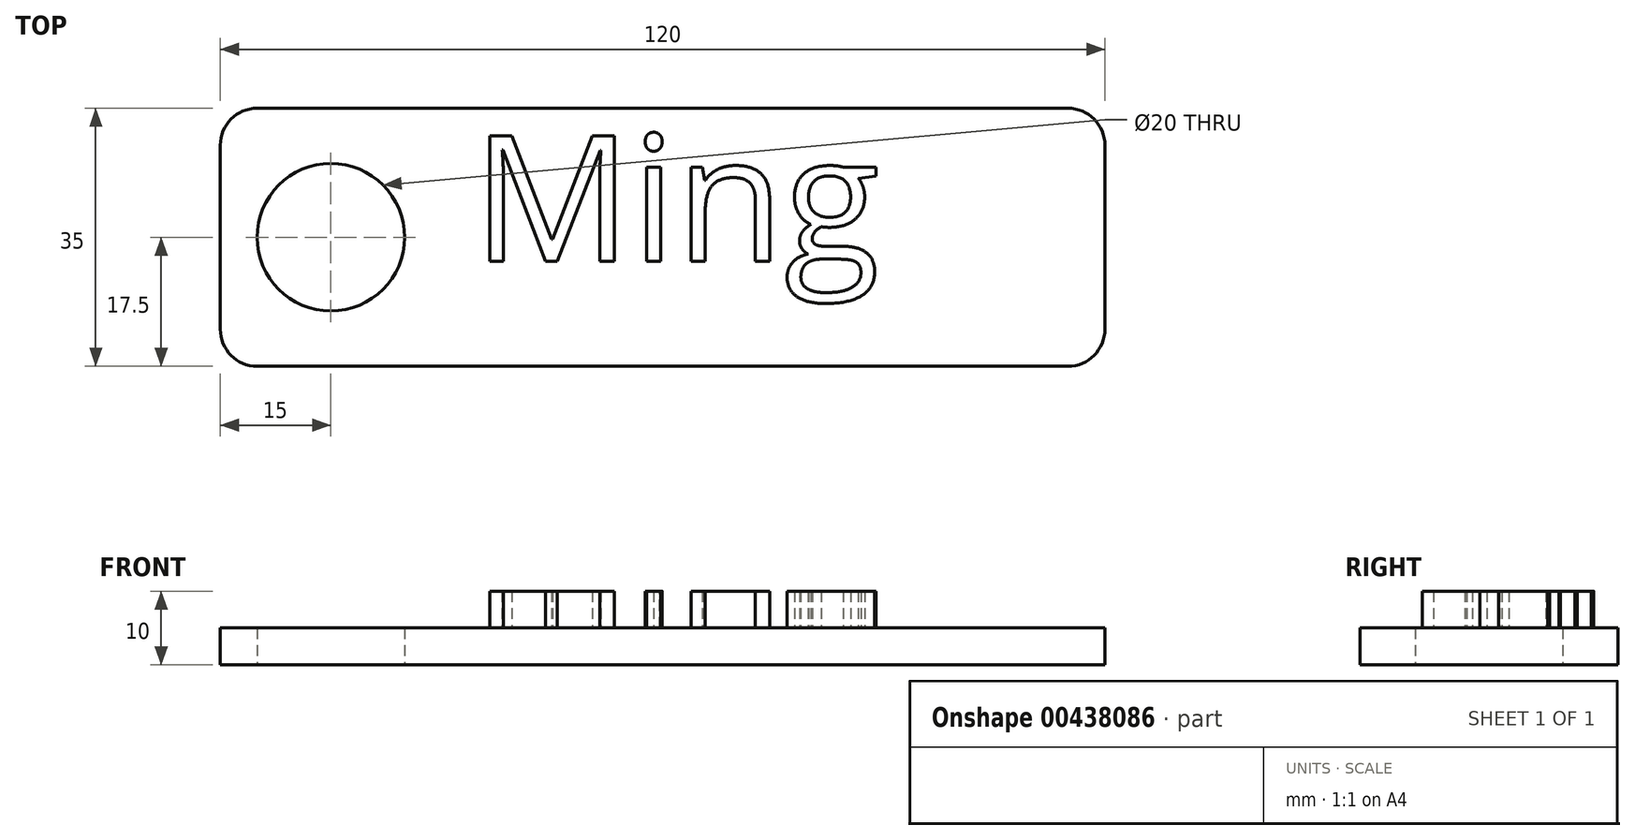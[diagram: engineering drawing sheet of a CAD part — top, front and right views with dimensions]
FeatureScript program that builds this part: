
annotation { "Feature Type Name" : "Feature", "Feature Type Description" : "" }
export const myFeature = defineFeature(function(context is Context, id is Id, definition is map)
    precondition{}
    {
        {
            var Q0;
            Q0=qCreatedBy(makeId("Top.planeOp"),FACE);
            var sketch = newSketch(context, id + "F0", { "sketchPlane" : qUnion([Q0])});
            skLineSegment(sketch, "E0.bottom", {"start": v(60, -17.5) * mm, "end": v(-60, -17.5) * mm});
            skLineSegment(sketch, "E0.top", {"start": v(60, 17.5) * mm, "end": v(-60, 17.5) * mm});
            skLineSegment(sketch, "E0.left", {"start": v(60, -17.5) * mm, "end": v(60, 17.5) * mm});
            skLineSegment(sketch, "E0.right", {"start": v(-60, -17.5) * mm, "end": v(-60, 17.5) * mm});
            skPoint(sketch, "E0.middle", {"position": v(0, 0) * mm});
            skCircle(sketch, "E1", {"center": v(-45, 0) * mm, "radius": 10 * mm});
            skSolve(sketch);
        }
        {
            var Q0;
            Q0=makeQuery(id+"F0.imprint","IMPRINT",FACE,{"disambiguationData":[TD([[makeQuery(id+"F0.imprint","IMPRINT",EDGE,{"derivedFrom":sQuery(id+"F0.wireOp",EDGE,"E0.bottom")}),-1.0]])]});
            extrude(context, id + "F1", {"entities" : qUnion([Q0]), "depth" : 5 * mm});
        }
        {
            var Q0;
            Q0=makeQuery(id+"F1.opExtrude","SWEPT_EDGE",EDGE,{"disambiguationData":[OSD([sQuery(id+"F0.wireOp",EDGE,"E0.top"),sQuery(id+"F0.wireOp",EDGE,"E0.right")])]});
            var Q1;
            Q1=makeQuery(id+"F1.opExtrude","SWEPT_EDGE",EDGE,{"disambiguationData":[OSD([sQuery(id+"F0.wireOp",EDGE,"E0.bottom"),sQuery(id+"F0.wireOp",EDGE,"E0.right")])]});
            var Q2;
            Q2=makeQuery(id+"F1.opExtrude","SWEPT_EDGE",EDGE,{"disambiguationData":[OSD([sQuery(id+"F0.wireOp",EDGE,"E0.bottom"),sQuery(id+"F0.wireOp",EDGE,"E0.left")])]});
            var Q3;
            Q3=makeQuery(id+"F1.opExtrude","SWEPT_EDGE",EDGE,{"disambiguationData":[OSD([sQuery(id+"F0.wireOp",EDGE,"E0.top"),sQuery(id+"F0.wireOp",EDGE,"E0.left")])]});
            fillet(context, id + "F2", {"entities" : qUnion([Q0, Q1, Q2, Q3]), "radius" : 5 * mm, "tangentPropagation" : true, "allowEdgeOverflow" : false});
        }
        {
            var Q0;
            Q0=makeQuery(id+"F1.opExtrude","CAP_FACE",FACE,{"disambiguationData":[OSD([sQuery(id+"F0.wireOp",EDGE,"E0.bottom"),sQuery(id+"F0.wireOp",EDGE,"E0.top"),sQuery(id+"F0.wireOp",EDGE,"E0.left"),sQuery(id+"F0.wireOp",EDGE,"E0.right"),sQuery(id+"F0.wireOp",EDGE,"E1")])],"isStart":false});
            var sketch = newSketch(context, id + "F3", { "sketchPlane" : qUnion([Q0])});
            skText(sketch, "E2", { "text": "Ming", "fontName": "OpenSans-Regular.ttf"});
            const initialGuessF3  = {"E2": [-0.02576, -0.00326, 1, 0, 0.01717]};
            skSetInitialGuess(sketch, initialGuessF3);
            skSolve(sketch);
        }
        {
            var Q0;
            Q0 = qSketchRegion(id + "F3", true);
            extrude(context, id + "F4", {"entities" : qUnion([Q0]), "operationType" : NewBodyOperationType.ADD, "depth" : 5 * mm});
        }
    });
